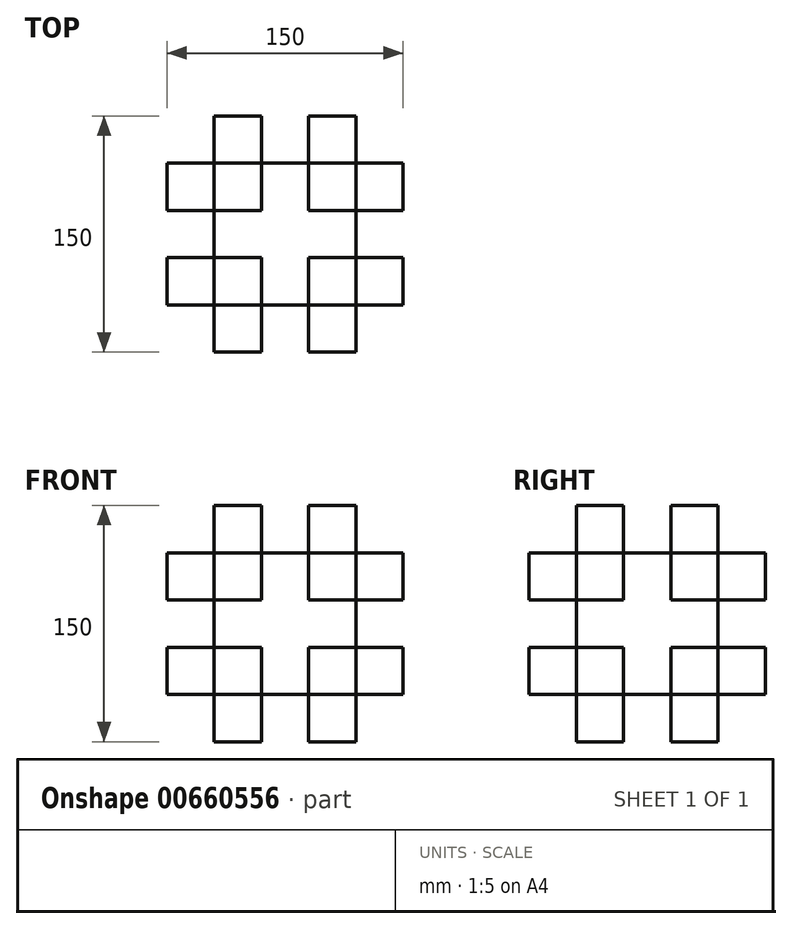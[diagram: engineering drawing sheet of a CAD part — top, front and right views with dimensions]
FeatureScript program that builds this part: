
annotation { "Feature Type Name" : "Feature", "Feature Type Description" : "" }
export const myFeature = defineFeature(function(context is Context, id is Id, definition is map)
    precondition{}
    {
        {
            var Q0;
            Q0=qCreatedBy(makeId("Top.planeOp"),FACE);
            var sketch = newSketch(context, id + "F0", { "sketchPlane" : qUnion([Q0])});
            skLineSegment(sketch, "E0.bottom", {"start": v(45, 45) * mm, "end": v(-45, 45) * mm});
            skLineSegment(sketch, "E0.top", {"start": v(45, -45) * mm, "end": v(-45, -45) * mm});
            skLineSegment(sketch, "E0.left", {"start": v(45, 45) * mm, "end": v(45, -45) * mm});
            skLineSegment(sketch, "E0.right", {"start": v(-45, 45) * mm, "end": v(-45, -45) * mm});
            skPoint(sketch, "E0.middle", {"position": v(0, 0) * mm});
            skSolve(sketch);
        }
        {
            var Q0;
            Q0 = qSketchRegion(id + "F0", true);
            extrude(context, id + "F1", {"entities" : qUnion([Q0]), "depth" : 90 * mm, "offsetDistance" : 25.4 * mm});
        }
        {
            var Q0;
            Q0=makeQuery(id+"F1.opExtrude","CAP_FACE",FACE,{"disambiguationData":[OSD([sQuery(id+"F0.wireOp",EDGE,"E0.bottom"),sQuery(id+"F0.wireOp",EDGE,"E0.top"),sQuery(id+"F0.wireOp",EDGE,"E0.left"),sQuery(id+"F0.wireOp",EDGE,"E0.right")])],"isStart":false});
            var sketch = newSketch(context, id + "F2", { "sketchPlane" : qUnion([Q0])});
            skLineSegment(sketch, "E1.bottom", {"start": v(-45, 45) * mm, "end": v(-15, 45) * mm});
            skLineSegment(sketch, "E1.top", {"start": v(-45, 15) * mm, "end": v(-15, 15) * mm});
            skLineSegment(sketch, "E1.left", {"start": v(-45, 45) * mm, "end": v(-45, 15) * mm});
            skLineSegment(sketch, "E1.right", {"start": v(-15, 45) * mm, "end": v(-15, 15) * mm});
            skLineSegment(sketch, "E2.MirrorCS", {"start": v(15, 45) * mm, "end": v(15, 15) * mm});
            skLineSegment(sketch, "E3.MirrorCS", {"start": v(45, 15) * mm, "end": v(15, 15) * mm});
            skLineSegment(sketch, "E4.MirrorCS", {"start": v(45, 45) * mm, "end": v(45, 15) * mm});
            skLineSegment(sketch, "E5.MirrorCS", {"start": v(45, 45) * mm, "end": v(15, 45) * mm});
            skLineSegment(sketch, "E6.MirrorCS", {"start": v(-45, -15) * mm, "end": v(-15, -15) * mm});
            skLineSegment(sketch, "E7.MirrorCS", {"start": v(-15, -45) * mm, "end": v(-15, -15) * mm});
            skLineSegment(sketch, "E8.MirrorCS", {"start": v(-45, -45) * mm, "end": v(-15, -45) * mm});
            skLineSegment(sketch, "E9.MirrorCS", {"start": v(-45, -45) * mm, "end": v(-45, -15) * mm});
            skLineSegment(sketch, "E10.MirrorCS", {"start": v(45, -45) * mm, "end": v(15, -45) * mm});
            skLineSegment(sketch, "E11.MirrorCS", {"start": v(15, -45) * mm, "end": v(15, -15) * mm});
            skLineSegment(sketch, "E12.MirrorCS", {"start": v(45, -15) * mm, "end": v(15, -15) * mm});
            skLineSegment(sketch, "E13.MirrorCS", {"start": v(45, -45) * mm, "end": v(45, -15) * mm});
            skSolve(sketch);
        }
        {
            var Q0;
            Q0 = qSketchRegion(id + "F2", true);
            extrude(context, id + "F3", {"entities" : qUnion([Q0]), "operationType" : NewBodyOperationType.ADD, "depth" : 30 * mm, "offsetDistance" : 25 * mm});
        }
        {
            var Q0;
            Q0=makeQuery(id+"F3.boolean.opBoolean","MERGE",FACE,{"derivedFrom":[makeQuery(id+"F1.opExtrude","SWEPT_FACE",FACE,{"disambiguationData":[OSD([sQuery(id+"F0.wireOp",EDGE,"E0.left")])]}),makeQuery(id+"F3.opExtrude","SWEPT_FACE",FACE,{"disambiguationData":[OSD([sQuery(id+"F2.wireOp",EDGE,"E4.MirrorCS")])]}),makeQuery(id+"F3.opExtrude","SWEPT_FACE",FACE,{"disambiguationData":[OSD([sQuery(id+"F2.wireOp",EDGE,"E13.MirrorCS")])]})]});
            var sketch = newSketch(context, id + "F4", { "sketchPlane" : qUnion([Q0])});
            skLineSegment(sketch, "E14.bottom", {"start": v(15, 90) * mm, "end": v(45, 90) * mm});
            skLineSegment(sketch, "E14.top", {"start": v(15, 60) * mm, "end": v(45, 60) * mm});
            skLineSegment(sketch, "E14.left", {"start": v(15, 90) * mm, "end": v(15, 60) * mm});
            skLineSegment(sketch, "E14.right", {"start": v(45, 90) * mm, "end": v(45, 60) * mm});
            skLineSegment(sketch, "E15.bottom", {"start": v(-15, 90) * mm, "end": v(-45, 90) * mm});
            skLineSegment(sketch, "E15.top", {"start": v(-15, 60) * mm, "end": v(-45, 60) * mm});
            skLineSegment(sketch, "E15.left", {"start": v(-15, 90) * mm, "end": v(-15, 60) * mm});
            skLineSegment(sketch, "E15.right", {"start": v(-45, 90) * mm, "end": v(-45, 60) * mm});
            skLineSegment(sketch, "E16.bottom", {"start": v(-45, 0) * mm, "end": v(-15, 0) * mm});
            skLineSegment(sketch, "E16.top", {"start": v(-45, 30) * mm, "end": v(-15, 30) * mm});
            skLineSegment(sketch, "E16.left", {"start": v(-45, 0) * mm, "end": v(-45, 30) * mm});
            skLineSegment(sketch, "E16.right", {"start": v(-15, 0) * mm, "end": v(-15, 30) * mm});
            skLineSegment(sketch, "E17.bottom", {"start": v(45, 0) * mm, "end": v(15, 0) * mm});
            skLineSegment(sketch, "E17.top", {"start": v(45, 30) * mm, "end": v(15, 30) * mm});
            skLineSegment(sketch, "E17.left", {"start": v(45, 0) * mm, "end": v(45, 30) * mm});
            skLineSegment(sketch, "E17.right", {"start": v(15, 0) * mm, "end": v(15, 30) * mm});
            skSolve(sketch);
        }
        {
            var Q0;
            Q0 = qSketchRegion(id + "F4", true);
            extrude(context, id + "F5", {"entities" : qUnion([Q0]), "operationType" : NewBodyOperationType.ADD, "depth" : 30 * mm, "offsetDistance" : 25 * mm});
        }
        {
            var Q0;
            Q0=makeQuery(id+"F5.boolean.opBoolean","MERGE",FACE,{"derivedFrom":[makeQuery(id+"F3.boolean.opBoolean","MERGE",FACE,{"derivedFrom":[makeQuery(id+"F1.opExtrude","SWEPT_FACE",FACE,{"disambiguationData":[OSD([sQuery(id+"F0.wireOp",EDGE,"E0.bottom")])]}),makeQuery(id+"F3.opExtrude","SWEPT_FACE",FACE,{"disambiguationData":[OSD([sQuery(id+"F2.wireOp",EDGE,"E1.bottom")])]}),makeQuery(id+"F3.opExtrude","SWEPT_FACE",FACE,{"disambiguationData":[OSD([sQuery(id+"F2.wireOp",EDGE,"E5.MirrorCS")])]})]}),makeQuery(id+"F5.opExtrude","SWEPT_FACE",FACE,{"disambiguationData":[OSD([sQuery(id+"F4.wireOp",EDGE,"E14.right")])]}),makeQuery(id+"F5.opExtrude","SWEPT_FACE",FACE,{"disambiguationData":[OSD([sQuery(id+"F4.wireOp",EDGE,"E17.left")])]})]});
            var sketch = newSketch(context, id + "F6", { "sketchPlane" : qUnion([Q0])});
            skLineSegment(sketch, "E18.bottom", {"start": v(-45, 90) * mm, "end": v(-15, 90) * mm});
            skLineSegment(sketch, "E18.top", {"start": v(-45, 60) * mm, "end": v(-15, 60) * mm});
            skLineSegment(sketch, "E18.left", {"start": v(-45, 90) * mm, "end": v(-45, 60) * mm});
            skLineSegment(sketch, "E18.right", {"start": v(-15, 90) * mm, "end": v(-15, 60) * mm});
            skLineSegment(sketch, "E19.bottom", {"start": v(-45, 30) * mm, "end": v(-15, 30) * mm});
            skLineSegment(sketch, "E19.top", {"start": v(-45, 0) * mm, "end": v(-15, 0) * mm});
            skLineSegment(sketch, "E19.left", {"start": v(-45, 30) * mm, "end": v(-45, 0) * mm});
            skLineSegment(sketch, "E19.right", {"start": v(-15, 30) * mm, "end": v(-15, 0) * mm});
            skLineSegment(sketch, "E20.bottom", {"start": v(45, 0) * mm, "end": v(15, 0) * mm});
            skLineSegment(sketch, "E20.top", {"start": v(45, 30) * mm, "end": v(15, 30) * mm});
            skLineSegment(sketch, "E20.left", {"start": v(45, 0) * mm, "end": v(45, 30) * mm});
            skLineSegment(sketch, "E20.right", {"start": v(15, 0) * mm, "end": v(15, 30) * mm});
            skLineSegment(sketch, "E21.bottom", {"start": v(15, 90) * mm, "end": v(45, 90) * mm});
            skLineSegment(sketch, "E21.top", {"start": v(15, 60) * mm, "end": v(45, 60) * mm});
            skLineSegment(sketch, "E21.left", {"start": v(15, 90) * mm, "end": v(15, 60) * mm});
            skLineSegment(sketch, "E21.right", {"start": v(45, 90) * mm, "end": v(45, 60) * mm});
            skSolve(sketch);
        }
        {
            var Q0;
            Q0 = qSketchRegion(id + "F6", true);
            extrude(context, id + "F7", {"entities" : qUnion([Q0]), "operationType" : NewBodyOperationType.ADD, "depth" : 30 * mm, "offsetDistance" : 25 * mm});
        }
        {
            var Q0;
            Q0=makeQuery(id+"F7.boolean.opBoolean","MERGE",FACE,{"derivedFrom":[makeQuery(id+"F3.boolean.opBoolean","MERGE",FACE,{"derivedFrom":[makeQuery(id+"F1.opExtrude","SWEPT_FACE",FACE,{"disambiguationData":[OSD([sQuery(id+"F0.wireOp",EDGE,"E0.right")])]}),makeQuery(id+"F3.opExtrude","SWEPT_FACE",FACE,{"disambiguationData":[OSD([sQuery(id+"F2.wireOp",EDGE,"E1.left")])]}),makeQuery(id+"F3.opExtrude","SWEPT_FACE",FACE,{"disambiguationData":[OSD([sQuery(id+"F2.wireOp",EDGE,"E9.MirrorCS")])]})]}),makeQuery(id+"F7.opExtrude","SWEPT_FACE",FACE,{"disambiguationData":[OSD([sQuery(id+"F6.wireOp",EDGE,"E20.left")])]}),makeQuery(id+"F7.opExtrude","SWEPT_FACE",FACE,{"disambiguationData":[OSD([sQuery(id+"F6.wireOp",EDGE,"E21.right")])]})]});
            var sketch = newSketch(context, id + "F8", { "sketchPlane" : qUnion([Q0])});
            skLineSegment(sketch, "E22.bottom", {"start": v(-45, 90) * mm, "end": v(-15, 90) * mm});
            skLineSegment(sketch, "E22.top", {"start": v(-45, 60) * mm, "end": v(-15, 60) * mm});
            skLineSegment(sketch, "E22.left", {"start": v(-45, 90) * mm, "end": v(-45, 60) * mm});
            skLineSegment(sketch, "E22.right", {"start": v(-15, 90) * mm, "end": v(-15, 60) * mm});
            skLineSegment(sketch, "E23.bottom", {"start": v(-45, 30) * mm, "end": v(-15, 30) * mm});
            skLineSegment(sketch, "E23.top", {"start": v(-45, 0) * mm, "end": v(-15, 0) * mm});
            skLineSegment(sketch, "E23.left", {"start": v(-45, 30) * mm, "end": v(-45, 0) * mm});
            skLineSegment(sketch, "E23.right", {"start": v(-15, 30) * mm, "end": v(-15, 0) * mm});
            skLineSegment(sketch, "E24.bottom", {"start": v(45, 0) * mm, "end": v(15, 0) * mm});
            skLineSegment(sketch, "E24.top", {"start": v(45, 30) * mm, "end": v(15, 30) * mm});
            skLineSegment(sketch, "E24.left", {"start": v(45, 0) * mm, "end": v(45, 30) * mm});
            skLineSegment(sketch, "E24.right", {"start": v(15, 0) * mm, "end": v(15, 30) * mm});
            skLineSegment(sketch, "E25.bottom", {"start": v(15, 90) * mm, "end": v(45, 90) * mm});
            skLineSegment(sketch, "E25.top", {"start": v(15, 60) * mm, "end": v(45, 60) * mm});
            skLineSegment(sketch, "E25.left", {"start": v(15, 90) * mm, "end": v(15, 60) * mm});
            skLineSegment(sketch, "E25.right", {"start": v(45, 90) * mm, "end": v(45, 60) * mm});
            skSolve(sketch);
        }
        {
            var Q0;
            Q0 = qSketchRegion(id + "F8", true);
            extrude(context, id + "F9", {"entities" : qUnion([Q0]), "operationType" : NewBodyOperationType.ADD, "depth" : 30 * mm, "offsetDistance" : 25 * mm});
        }
        {
            var Q0;
            Q0=makeQuery(id+"F9.boolean.opBoolean","MERGE",FACE,{"derivedFrom":[makeQuery(id+"F5.boolean.opBoolean","MERGE",FACE,{"derivedFrom":[makeQuery(id+"F3.boolean.opBoolean","MERGE",FACE,{"derivedFrom":[makeQuery(id+"F1.opExtrude","SWEPT_FACE",FACE,{"disambiguationData":[OSD([sQuery(id+"F0.wireOp",EDGE,"E0.top")])]}),makeQuery(id+"F3.opExtrude","SWEPT_FACE",FACE,{"disambiguationData":[OSD([sQuery(id+"F2.wireOp",EDGE,"E8.MirrorCS")])]}),makeQuery(id+"F3.opExtrude","SWEPT_FACE",FACE,{"disambiguationData":[OSD([sQuery(id+"F2.wireOp",EDGE,"E10.MirrorCS")])]})]}),makeQuery(id+"F5.opExtrude","SWEPT_FACE",FACE,{"disambiguationData":[OSD([sQuery(id+"F4.wireOp",EDGE,"E15.right")])]}),makeQuery(id+"F5.opExtrude","SWEPT_FACE",FACE,{"disambiguationData":[OSD([sQuery(id+"F4.wireOp",EDGE,"E16.left")])]})]}),makeQuery(id+"F9.opExtrude","SWEPT_FACE",FACE,{"disambiguationData":[OSD([sQuery(id+"F8.wireOp",EDGE,"E24.left")])]}),makeQuery(id+"F9.opExtrude","SWEPT_FACE",FACE,{"disambiguationData":[OSD([sQuery(id+"F8.wireOp",EDGE,"E25.right")])]})]});
            var sketch = newSketch(context, id + "F10", { "sketchPlane" : qUnion([Q0])});
            skLineSegment(sketch, "E26.bottom", {"start": v(-45, 90) * mm, "end": v(-15, 90) * mm});
            skLineSegment(sketch, "E26.top", {"start": v(-45, 60) * mm, "end": v(-15, 60) * mm});
            skLineSegment(sketch, "E26.left", {"start": v(-45, 90) * mm, "end": v(-45, 60) * mm});
            skLineSegment(sketch, "E26.right", {"start": v(-15, 90) * mm, "end": v(-15, 60) * mm});
            skLineSegment(sketch, "E27.bottom", {"start": v(-45, 30) * mm, "end": v(-15, 30) * mm});
            skLineSegment(sketch, "E27.top", {"start": v(-45, 0) * mm, "end": v(-15, 0) * mm});
            skLineSegment(sketch, "E27.left", {"start": v(-45, 30) * mm, "end": v(-45, 0) * mm});
            skLineSegment(sketch, "E27.right", {"start": v(-15, 30) * mm, "end": v(-15, 0) * mm});
            skLineSegment(sketch, "E28.bottom", {"start": v(45, 30) * mm, "end": v(15, 30) * mm});
            skLineSegment(sketch, "E28.top", {"start": v(45, 0) * mm, "end": v(15, 0) * mm});
            skLineSegment(sketch, "E28.left", {"start": v(45, 30) * mm, "end": v(45, 0) * mm});
            skLineSegment(sketch, "E28.right", {"start": v(15, 30) * mm, "end": v(15, 0) * mm});
            skLineSegment(sketch, "E29.bottom", {"start": v(45, 60) * mm, "end": v(15, 60) * mm});
            skLineSegment(sketch, "E29.top", {"start": v(45, 90) * mm, "end": v(15, 90) * mm});
            skLineSegment(sketch, "E29.left", {"start": v(45, 60) * mm, "end": v(45, 90) * mm});
            skLineSegment(sketch, "E29.right", {"start": v(15, 60) * mm, "end": v(15, 90) * mm});
            skSolve(sketch);
        }
        {
            var Q0;
            Q0 = qSketchRegion(id + "F10", true);
            extrude(context, id + "F11", {"entities" : qUnion([Q0]), "operationType" : NewBodyOperationType.ADD, "depth" : 30 * mm, "offsetDistance" : 25 * mm});
        }
        {
            var Q0;
            Q0=makeQuery(id+"F11.boolean.opBoolean","MERGE",FACE,{"derivedFrom":[makeQuery(id+"F9.boolean.opBoolean","MERGE",FACE,{"derivedFrom":[makeQuery(id+"F7.boolean.opBoolean","MERGE",FACE,{"derivedFrom":[makeQuery(id+"F5.boolean.opBoolean","MERGE",FACE,{"derivedFrom":[makeQuery(id+"F1.opExtrude","CAP_FACE",FACE,{"disambiguationData":[OSD([sQuery(id+"F0.wireOp",EDGE,"E0.bottom"),sQuery(id+"F0.wireOp",EDGE,"E0.top"),sQuery(id+"F0.wireOp",EDGE,"E0.left"),sQuery(id+"F0.wireOp",EDGE,"E0.right")])],"isStart":true}),makeQuery(id+"F5.opExtrude","SWEPT_FACE",FACE,{"disambiguationData":[OSD([sQuery(id+"F4.wireOp",EDGE,"E16.bottom")])]}),makeQuery(id+"F5.opExtrude","SWEPT_FACE",FACE,{"disambiguationData":[OSD([sQuery(id+"F4.wireOp",EDGE,"E17.bottom")])]})]}),makeQuery(id+"F7.opExtrude","SWEPT_FACE",FACE,{"disambiguationData":[OSD([sQuery(id+"F6.wireOp",EDGE,"E19.top")])]}),makeQuery(id+"F7.opExtrude","SWEPT_FACE",FACE,{"disambiguationData":[OSD([sQuery(id+"F6.wireOp",EDGE,"E20.bottom")])]})]}),makeQuery(id+"F9.opExtrude","SWEPT_FACE",FACE,{"disambiguationData":[OSD([sQuery(id+"F8.wireOp",EDGE,"E23.top")])]}),makeQuery(id+"F9.opExtrude","SWEPT_FACE",FACE,{"disambiguationData":[OSD([sQuery(id+"F8.wireOp",EDGE,"E24.bottom")])]})]}),makeQuery(id+"F11.opExtrude","SWEPT_FACE",FACE,{"disambiguationData":[OSD([sQuery(id+"F10.wireOp",EDGE,"E27.top")])]}),makeQuery(id+"F11.opExtrude","SWEPT_FACE",FACE,{"disambiguationData":[OSD([sQuery(id+"F10.wireOp",EDGE,"E28.top")])]})]});
            var sketch = newSketch(context, id + "F12", { "sketchPlane" : qUnion([Q0])});
            skLineSegment(sketch, "E30.bottom", {"start": v(-45, 45) * mm, "end": v(-15, 45) * mm});
            skLineSegment(sketch, "E30.top", {"start": v(-45, 15) * mm, "end": v(-15, 15) * mm});
            skLineSegment(sketch, "E30.left", {"start": v(-45, 45) * mm, "end": v(-45, 15) * mm});
            skLineSegment(sketch, "E30.right", {"start": v(-15, 45) * mm, "end": v(-15, 15) * mm});
            skLineSegment(sketch, "E31.bottom", {"start": v(-45, -15) * mm, "end": v(-15, -15) * mm});
            skLineSegment(sketch, "E31.top", {"start": v(-45, -45) * mm, "end": v(-15, -45) * mm});
            skLineSegment(sketch, "E31.left", {"start": v(-45, -15) * mm, "end": v(-45, -45) * mm});
            skLineSegment(sketch, "E31.right", {"start": v(-15, -15) * mm, "end": v(-15, -45) * mm});
            skLineSegment(sketch, "E32.bottom", {"start": v(15, -45) * mm, "end": v(45, -45) * mm});
            skLineSegment(sketch, "E32.top", {"start": v(15, -15) * mm, "end": v(45, -15) * mm});
            skLineSegment(sketch, "E32.left", {"start": v(15, -45) * mm, "end": v(15, -15) * mm});
            skLineSegment(sketch, "E32.right", {"start": v(45, -45) * mm, "end": v(45, -15) * mm});
            skLineSegment(sketch, "E33.bottom", {"start": v(45, 15) * mm, "end": v(15, 15) * mm});
            skLineSegment(sketch, "E33.top", {"start": v(45, 45) * mm, "end": v(15, 45) * mm});
            skLineSegment(sketch, "E33.left", {"start": v(45, 15) * mm, "end": v(45, 45) * mm});
            skLineSegment(sketch, "E33.right", {"start": v(15, 15) * mm, "end": v(15, 45) * mm});
            skSolve(sketch);
        }
        {
            var Q0;
            Q0 = qSketchRegion(id + "F12", true);
            extrude(context, id + "F13", {"entities" : qUnion([Q0]), "operationType" : NewBodyOperationType.ADD, "depth" : 30 * mm, "offsetDistance" : 25 * mm});
        }
    });
